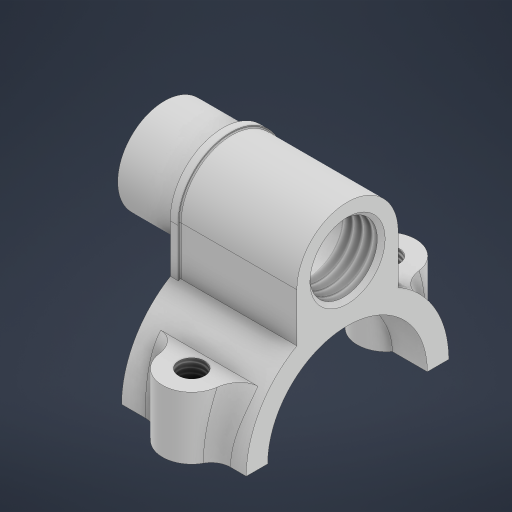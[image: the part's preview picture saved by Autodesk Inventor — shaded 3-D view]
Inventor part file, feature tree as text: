
AUTODESK INVENTOR PART (.ipt)
format: ipt  version: 2023 (Build 270158000, 158)  size: 435,712 bytes
history: native  units: mm
features: sketch x10, extrude x6, chamfer x5, other x4, hole x2, fillet x1
ambient origin geometry x8: Origin, YZ Plane, XZ Plane, XY Plane, X Axis, Y Axis, Z Axis, Center Point
bodies: Body1 (feature_tree)
feature tree (28):
  other  "Bryła1"
  extrude  "Wyciągnięcie proste1"  Depth=26.0mm
  extrude  "Wyciągnięcie proste2"  Depth=20.5mm
  other  "Zaokrąglenie powierzchni2"
  extrude  "Wyciągnięcie proste3"  Depth=26.0mm
  hole  "Otwór2"  [1 undecoded]
  chamfer  "Faza2"  Distance=13.5mm
  chamfer  "Faza3"  Distance=2.0mm
  sketch  "Szkic6"
  sketch  "Szkic7"
  extrude  "Wyciągnięcie proste4"  Depth=35.0mm
  extrude  "Wyciągnięcie proste5"  Depth=0.268mm
  chamfer  "Faza4"  Distance=24.0mm
  other  "Zaokrąglenie powierzchni3"
  extrude  "Wyciągnięcie proste6"  Depth=15.0mm TaperAngle=0.0deg
  fillet  "Zaokrąglenie1"  Radius=1.0mm
  hole  "Otwór3"  [1 undecoded]
  chamfer  "Faza5"  Distance=10.0mm
  chamfer  "Faza6"  Distance=15.0mm
  sketch  "Szkic1"
  sketch  "Szkic3"
  sketch  "Szkic4"
  sketch  "Szkic5"
  sketch  "Szkic8"
  sketch  "Szkic9"
  sketch  "Szkic10"
  sketch  "Szkic11"
  other  "Rzutuj krawędzie tnące1"
note: 2 required parameter values undecoded (feature->parameter linkage not recoverable at this tier; creation-order binding heuristic only, values carry confidence <= 0.55)
